# Revit family: Пергола-качели «Сомниум» Арт 13024
name_source: partatom
category: Антураж
revit_build: Autodesk Revit 2018 (Build: 20180423_1000(x64)
units: mm (PartAtom-declared; Revit-internal decimal feet)

## family parameters
Всегда вертикально = Да
Источник визуального образа = Геометрия семейства
На основе рабочей плоскости = Нет
Общий = Нет
При загрузке вырезать с полостями = Нет
Точка расчета площади = Нет

## types (2) — shared parameters
URL = https://hobbyka.ru
Артикул товара = Арт. 13024
Высота = 2200 мм
Группа модели = Садовая и дачная мебель
Длина = 2500 мм
Изготовитель = ООО «Хоббика»
Изображение типоразмера = Пергола-качели «Сомниум» Арт 13024.jpg
Материал изделия = Дерево
Ширина = 1500 мм

## per-type parameters (varying)
| type | Лиственница | Сосна | Цвет отделки |
| Пергола-качели «Сомниум». Версия из сосны | Нет | Да | Сосна |
| Пергола-качели «Сомниум». Версия из лиственницы | Да | Нет | Лиственница |

note: column(s) folded — value = type name in every type: Описание
